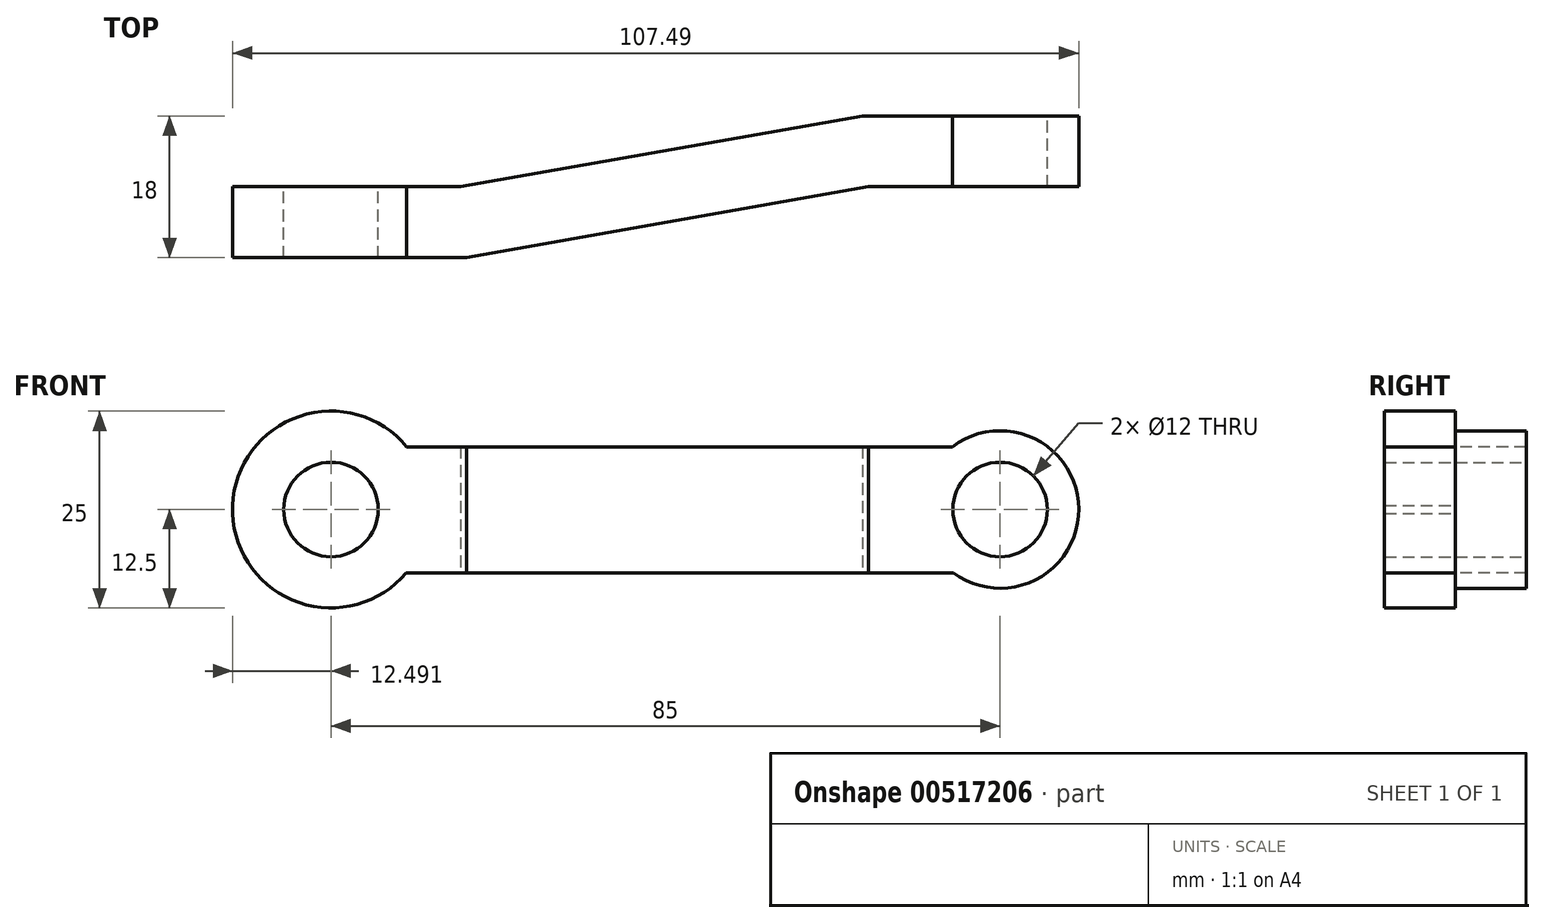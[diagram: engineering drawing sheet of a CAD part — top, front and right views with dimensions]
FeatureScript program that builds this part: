
annotation { "Feature Type Name" : "Feature", "Feature Type Description" : "" }
export const myFeature = defineFeature(function(context is Context, id is Id, definition is map)
    precondition{}
    {
        {
            var Q0;
            Q0=qCreatedBy(makeId("Front.planeOp"),FACE);
            var sketch = newSketch(context, id + "F0", { "sketchPlane" : qUnion([Q0])});
            skCircle(sketch, "E0", {"center": v(-44, 0) * mm, "radius": 12.5 * mm});
            skCircle(sketch, "E1", {"center": v(41, 0) * mm, "radius": 10 * mm});
            skLineSegment(sketch, "E2", {"start": v(-34.44, -8.04) * mm, "end": v(35.05, -8.04) * mm});
            skLineSegment(sketch, "E3", {"start": v(-34.37, 7.96) * mm, "end": v(34.94, 7.96) * mm});
            skCircle(sketch, "E4", {"center": v(-44, 0) * mm, "radius": 6 * mm});
            skCircle(sketch, "E5", {"center": v(41, 0) * mm, "radius": 6 * mm});
            skSolve(sketch);
        }
        {
            var Q0;
            Q0=makeQuery(id+"F0.imprint","IMPRINT",FACE,{"disambiguationData":[TD([[makeQuery(id+"F0.imprint","IMPRINT",EDGE,{"derivedFrom":sQuery(id+"F0.wireOp",EDGE,"E4")}),-1.0]])]});
            var Q1;
            {var subQ0=sQuery(id+"F0.wireOp",EDGE,"E2");Q1=makeQuery(id+"F0.imprint","IMPRINT",FACE,{"disambiguationData":[TD([[makeQuery(id+"F0.imprint","IMPRINT",EDGE,{"derivedFrom":subQ0}),1.0]])]});}
            var Q2;
            Q2=makeQuery(id+"F0.imprint","IMPRINT",FACE,{"disambiguationData":[TD([[makeQuery(id+"F0.imprint","IMPRINT",EDGE,{"derivedFrom":sQuery(id+"F0.wireOp",EDGE,"E5")}),-1.0]])]});
            extrude(context, id + "F1", {"entities" : qUnion([Q0, Q1, Q2]), "depth" : 25 * mm, "offsetDistance" : 25 * mm});
        }
        {
            var Q0;
            Q0=qCreatedBy(makeId("Top.planeOp"),FACE);
            var sketch = newSketch(context, id + "F2", { "sketchPlane" : qUnion([Q0])});
            skLineSegment(sketch, "E6", {"start": v(-56.5, -9) * mm, "end": v(-27.55, -9) * mm});
            skLineSegment(sketch, "E7", {"start": v(-27.55, -9) * mm, "end": v(23.49, 0) * mm});
            skLineSegment(sketch, "E8", {"start": v(23.49, 0) * mm, "end": v(51.13, 0) * mm});
            skLineSegment(sketch, "E9.0", {"start": v(24.27, -9) * mm, "end": v(51.13, -9) * mm});
            skLineSegment(sketch, "E9.1", {"start": v(-26.77, -18) * mm, "end": v(24.27, -9) * mm});
            skLineSegment(sketch, "E9.2", {"start": v(-56.5, -18) * mm, "end": v(-26.77, -18) * mm});
            skLineSegment(sketch, "E10", {"start": v(-56.5, -9) * mm, "end": v(-56.5, -18.32) * mm});
            skLineSegment(sketch, "E11", {"start": v(51.13, 0) * mm, "end": v(51.13, -9) * mm});
            skPoint(sketch, "E12", {"position": v(43.49, 0) * mm});
            skLineSegment(sketch, "E13", {"start": v(-56.5, -25) * mm, "end": v(-56.5, 0) * mm});
            skSolve(sketch);
        }
        {
            var Q0;
            Q0 = qSketchRegion(id + "F2", true);
            extrude(context, id + "F3", {"entities" : qUnion([Q0]), "operationType" : NewBodyOperationType.INTERSECT, "endBound" : BoundingType.SYMMETRIC, "depth" : 25 * mm, "offsetDistance" : 25 * mm});
        }
    });
